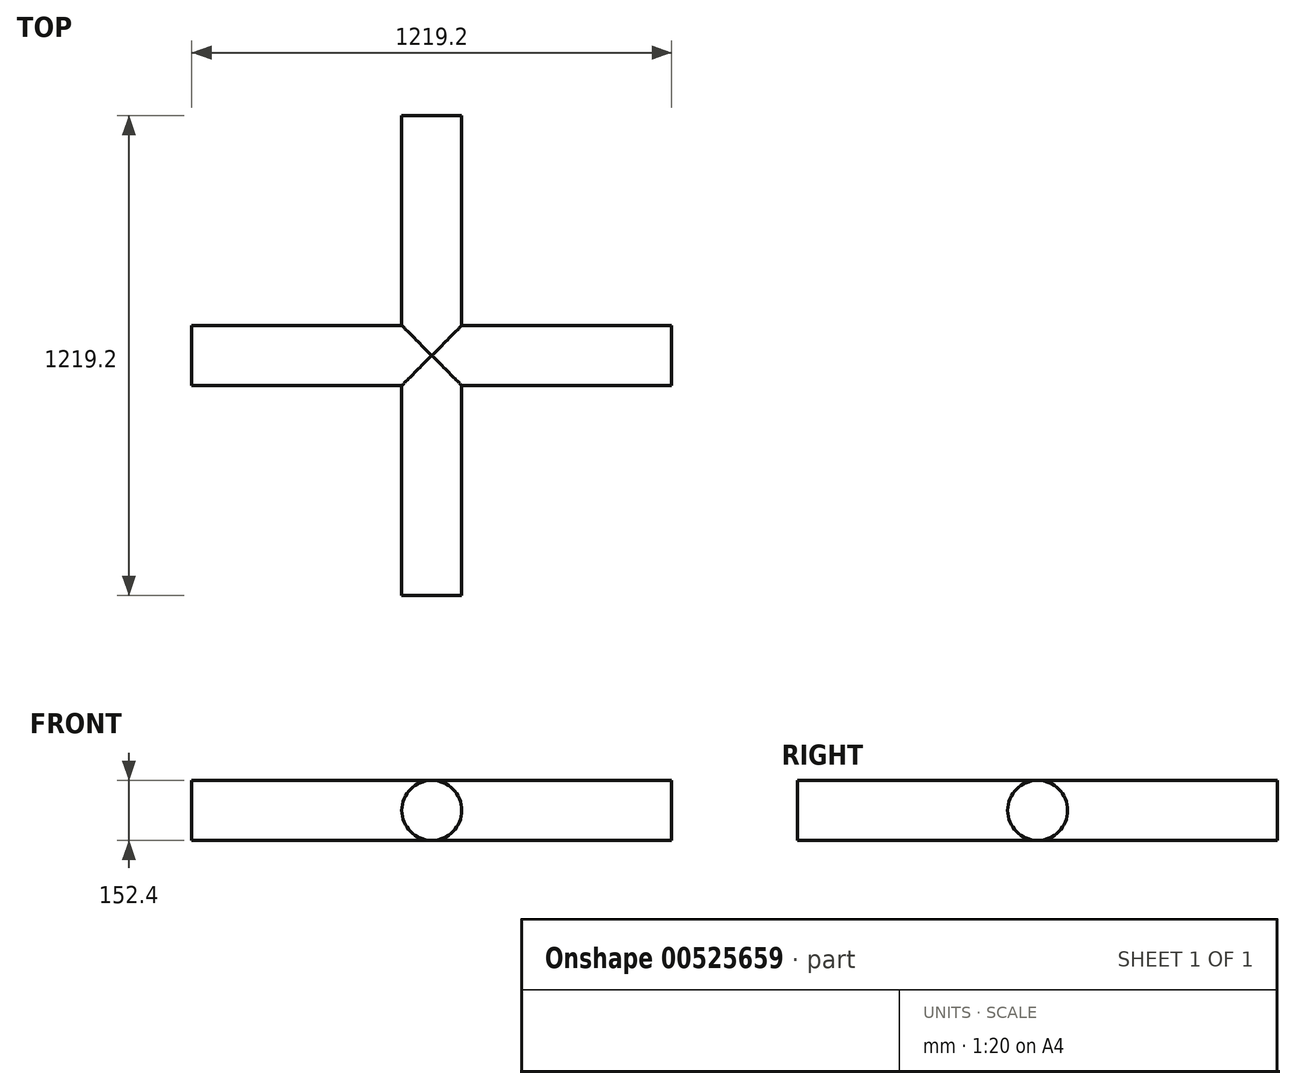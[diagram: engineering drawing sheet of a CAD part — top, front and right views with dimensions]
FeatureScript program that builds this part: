
annotation { "Feature Type Name" : "Feature", "Feature Type Description" : "" }
export const myFeature = defineFeature(function(context is Context, id is Id, definition is map)
    precondition{}
    {
        {
            var Q0;
            Q0=qCreatedBy(makeId("Front.planeOp"),FACE);
            var sketch = newSketch(context, id + "F0", { "sketchPlane" : qUnion([Q0])});
            skCircle(sketch, "E0", {"center": v(0, 0) * mm, "radius": 76.2 * mm});
            skSolve(sketch);
        }
        {
            var Q0;
            Q0=makeQuery(id+"F0.imprint","IMPRINT",FACE,{"disambiguationData":[TD([[makeQuery(id+"F0.imprint","IMPRINT",EDGE,{"derivedFrom":sQuery(id+"F0.wireOp",EDGE,"E0")}),1.0]])]});
            extrude(context, id + "F1", {"entities" : qUnion([Q0]), "depth" : 609.6 * mm, "offsetDistance" : 25.4 * mm, "hasSecondDirection" : true, "secondDirectionOppositeDirection" : true, "secondDirectionDepth" : 609.6 * mm});
        }
        {
            var Q0;
            Q0=qCreatedBy(makeId("Right.planeOp"),FACE);
            var sketch = newSketch(context, id + "F2", { "sketchPlane" : qUnion([Q0])});
            skCircle(sketch, "E1", {"center": v(0, 0) * mm, "radius": 76.2 * mm});
            skSolve(sketch);
        }
        {
            var Q0;
            Q0 = qSketchRegion(id + "F2", true);
            extrude(context, id + "F3", {"entities" : qUnion([Q0]), "operationType" : NewBodyOperationType.ADD, "depth" : 609.6 * mm, "offsetDistance" : 25.4 * mm, "hasSecondDirection" : true, "secondDirectionOppositeDirection" : true, "secondDirectionDepth" : 609.6 * mm});
        }
    });
